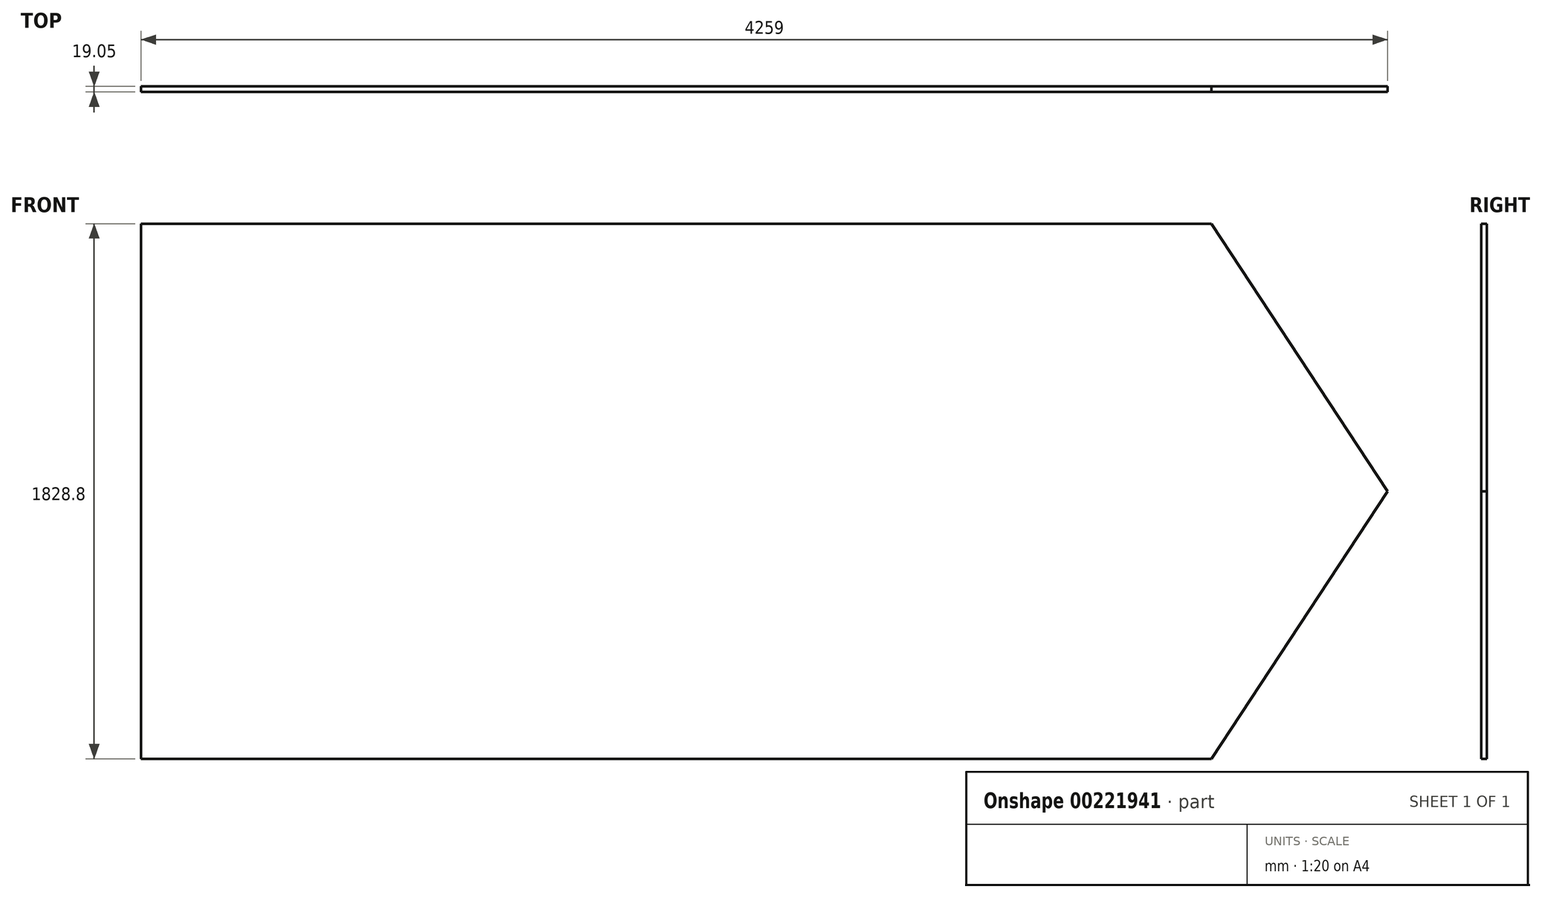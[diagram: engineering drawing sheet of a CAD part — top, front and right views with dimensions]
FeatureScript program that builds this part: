
annotation { "Feature Type Name" : "Feature", "Feature Type Description" : "" }
export const myFeature = defineFeature(function(context is Context, id is Id, definition is map)
    precondition{}
    {
        {
            var Q0;
            Q0=qCreatedBy(makeId("Front.planeOp"),FACE);
            var sketch = newSketch(context, id + "F0", { "sketchPlane" : qUnion([Q0])});
            skLineSegment(sketch, "E0.bottom", {"start": v(-1852.13, 504.33) * mm, "end": v(1805.47, 504.33) * mm});
            skLineSegment(sketch, "E0.top", {"start": v(-1852.13, -1324.47) * mm, "end": v(1805.47, -1324.47) * mm});
            skLineSegment(sketch, "E0.left", {"start": v(-1852.13, 504.33) * mm, "end": v(-1852.13, -1324.47) * mm});
            skLineSegment(sketch, "E0.right", {"start": v(1805.47, 504.33) * mm, "end": v(1805.47, -1324.47) * mm});
            skLineSegment(sketch, "E1", {"start": v(1805.47, 504.33) * mm, "end": v(2406.87, -410.07) * mm});
            skLineSegment(sketch, "E2", {"start": v(1805.47, -1324.47) * mm, "end": v(2406.87, -410.07) * mm});
            skSolve(sketch);
        }
        {
            var Q0;
            Q0=makeQuery(id+"F0.imprint","IMPRINT",FACE,{"disambiguationData":[TD([[makeQuery(id+"F0.imprint","IMPRINT",EDGE,{"derivedFrom":sQuery(id+"F0.wireOp",EDGE,"E0.right")}),1.0]])]});
            var Q1;
            Q1=makeQuery(id+"F0.imprint","IMPRINT",FACE,{"disambiguationData":[TD([[makeQuery(id+"F0.imprint","IMPRINT",EDGE,{"derivedFrom":sQuery(id+"F0.wireOp",EDGE,"E0.bottom")}),-1.0]])]});
            extrude(context, id + "F1", {"entities" : qUnion([Q0, Q1]), "depth" : 19.05 * mm});
        }
    });
